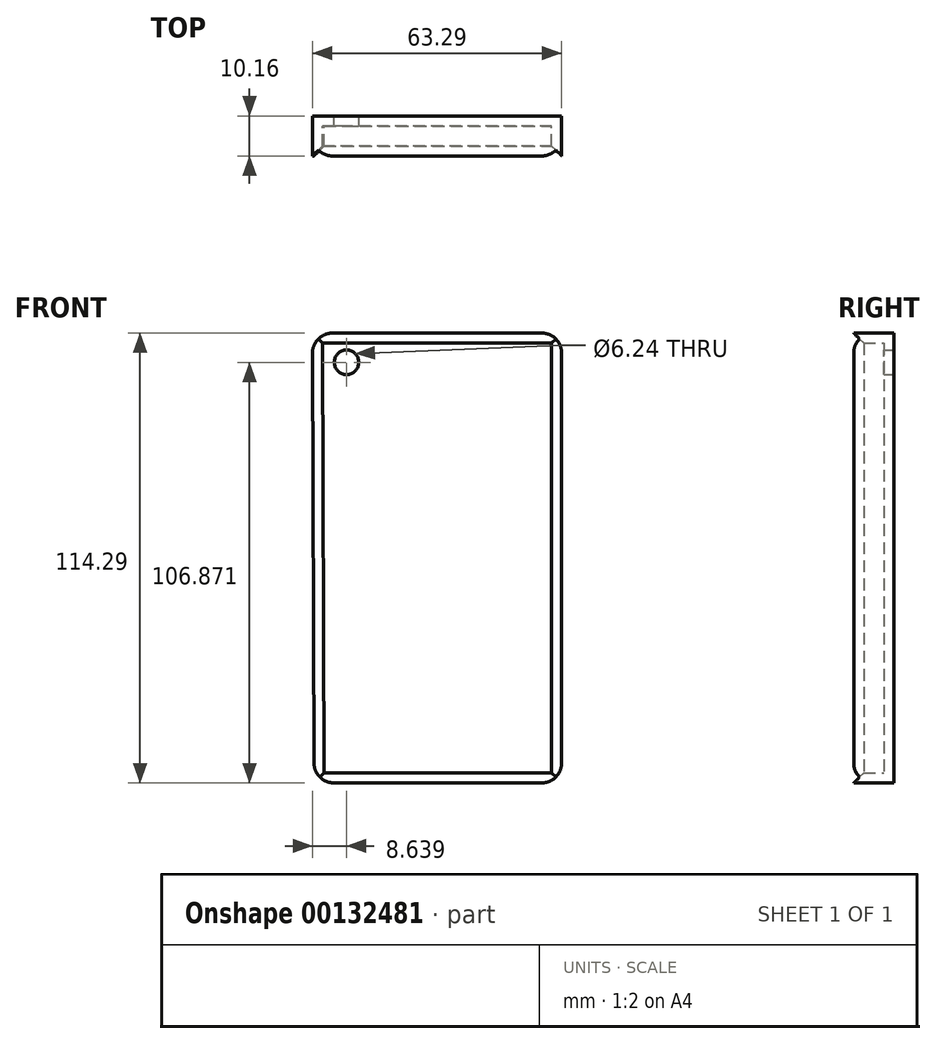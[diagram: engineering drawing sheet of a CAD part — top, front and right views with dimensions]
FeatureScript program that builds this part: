
annotation { "Feature Type Name" : "Feature", "Feature Type Description" : "" }
export const myFeature = defineFeature(function(context is Context, id is Id, definition is map)
    precondition{}
    {
        {
            var Q0;
            Q0=qCreatedBy(makeId("Front.planeOp"),FACE);
            var sketch = newSketch(context, id + "F0", { "sketchPlane" : qUnion([Q0])});
            skLineSegment(sketch, "E0", {"start": v(-75.68, -57.38) * mm, "end": v(-12.78, -57.38) * mm});
            skLineSegment(sketch, "E1", {"start": v(-12.78, -57.38) * mm, "end": v(-12.78, 56.91) * mm});
            skLineSegment(sketch, "E2", {"start": v(-12.78, 56.91) * mm, "end": v(-76.1, 56.91) * mm});
            skLineSegment(sketch, "E3", {"start": v(-76.1, 56.91) * mm, "end": v(-75.68, -57.38) * mm});
            skSolve(sketch);
        }
        {
            var Q0;
            Q0=makeQuery(id+"F0.imprint","IMPRINT",FACE,{"disambiguationData":[TD([[makeQuery(id+"F0.imprint","IMPRINT",EDGE,{"derivedFrom":sQuery(id+"F0.wireOp",EDGE,"E0")}),1.0]])]});
            extrude(context, id + "F1", {"entities" : qUnion([Q0]), "depth" : 12.7 * mm});
        }
        {
            var Q0;
            Q0=makeQuery(id+"F1.opExtrude","CAP_FACE",FACE,{"disambiguationData":[OSD([sQuery(id+"F0.wireOp",EDGE,"E0"),sQuery(id+"F0.wireOp",EDGE,"E1"),sQuery(id+"F0.wireOp",EDGE,"E2"),sQuery(id+"F0.wireOp",EDGE,"E3")])],"isStart":false});
            shell(context, id + "F2", {"entities" : qUnion([Q0]), "thickness" : 2.54 * mm});
        }
        {
            var Q0;
            Q0=makeQuery(id+"F1.opExtrude","SWEPT_EDGE",EDGE,{"disambiguationData":[OSD([sQuery(id+"F0.wireOp",EDGE,"E1"),sQuery(id+"F0.wireOp",EDGE,"E2")])]});
            var Q1;
            Q1=makeQuery(id+"F1.opExtrude","SWEPT_EDGE",EDGE,{"disambiguationData":[OSD([sQuery(id+"F0.wireOp",EDGE,"E2"),sQuery(id+"F0.wireOp",EDGE,"E3")])]});
            var Q2;
            Q2=makeQuery(id+"F1.opExtrude","SWEPT_EDGE",EDGE,{"disambiguationData":[OSD([sQuery(id+"F0.wireOp",EDGE,"E0"),sQuery(id+"F0.wireOp",EDGE,"E1")])]});
            var Q3;
            Q3=makeQuery(id+"F1.opExtrude","SWEPT_EDGE",EDGE,{"disambiguationData":[OSD([sQuery(id+"F0.wireOp",EDGE,"E0"),sQuery(id+"F0.wireOp",EDGE,"E3")])]});
            fillet(context, id + "F3", {"entities" : qUnion([Q0, Q1, Q2, Q3]), "radius" : 5.08 * mm, "tangentPropagation" : true, "allowEdgeOverflow" : false});
        }
        {
            var Q0;
            {var subQ0=sQuery(id+"F0.wireOp",EDGE,"E0");Q0=makeQuery(id+"F2.opShell","OFFSET_EDGE",EDGE,{"disambiguationData":[OSD([subQ0]),TDD([makeQuery(id+"F1.opExtrude","CAP_EDGE",EDGE,{"disambiguationData":[OSD([subQ0])],"isStart":false})])]});}
            var Q1;
            {var subQ0=sQuery(id+"F0.wireOp",EDGE,"E2");Q1=makeQuery(id+"F2.opShell","OFFSET_EDGE",EDGE,{"disambiguationData":[OSD([subQ0]),TDD([makeQuery(id+"F1.opExtrude","CAP_EDGE",EDGE,{"disambiguationData":[OSD([subQ0])],"isStart":false})])]});}
            var Q2;
            {var subQ0=sQuery(id+"F0.wireOp",EDGE,"E1");Q2=makeQuery(id+"F2.opShell","OFFSET_EDGE",EDGE,{"disambiguationData":[OSD([subQ0]),TDD([makeQuery(id+"F1.opExtrude","CAP_EDGE",EDGE,{"disambiguationData":[OSD([subQ0])],"isStart":false})])]});}
            var Q3;
            {var subQ0=sQuery(id+"F0.wireOp",EDGE,"E3");Q3=makeQuery(id+"F2.opShell","OFFSET_EDGE",EDGE,{"disambiguationData":[OSD([subQ0]),TDD([makeQuery(id+"F1.opExtrude","CAP_EDGE",EDGE,{"disambiguationData":[OSD([subQ0])],"isStart":false})])]});}
            chamfer(context, id + "F4", {"entities" : qUnion([Q0, Q1, Q2, Q3]), "width" : 5.08 * mm, "tangentPropagation" : true});
        }
        {
            var Q0;
            Q0=makeQuery(id+"F1.opExtrude","CAP_FACE",FACE,{"disambiguationData":[OSD([sQuery(id+"F0.wireOp",EDGE,"E0"),sQuery(id+"F0.wireOp",EDGE,"E1"),sQuery(id+"F0.wireOp",EDGE,"E2"),sQuery(id+"F0.wireOp",EDGE,"E3")])],"isStart":true});
            var sketch = newSketch(context, id + "F5", { "sketchPlane" : qUnion([Q0])});
            skCircle(sketch, "E4", {"center": v(67.43, 49.5) * mm, "radius": 3.12 * mm});
            skSolve(sketch);
        }
        {
            var Q0;
            Q0=makeQuery(id+"F5.imprint","IMPRINT",FACE,{"disambiguationData":[TD([[makeQuery(id+"F5.imprint","IMPRINT",EDGE,{"derivedFrom":sQuery(id+"F5.wireOp",EDGE,"E4")}),1.0]])]});
            extrude(context, id + "F6", {"entities" : qUnion([Q0]), "operationType" : NewBodyOperationType.REMOVE, "oppositeDirection" : true, "depth" : 25.4 * mm});
        }
    });
